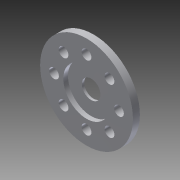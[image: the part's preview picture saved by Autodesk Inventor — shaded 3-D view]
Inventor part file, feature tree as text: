
AUTODESK INVENTOR PART (.ipt)
format: ipt  version: 2013 (Build 170138000, 138)  size: 110,592 bytes
history: native  units: mm
features: sketch x3, hole x2, extrude x1, pattern_circular x1
ambient origin geometry x8: Origin, YZ Plane, XZ Plane, XY Plane, X Axis, Y Axis, Z Axis, Center Point
feature tree (7):
  extrude  "押し出し2"  Depth=20.0mm
  hole  "穴2"  [1 undecoded]
  hole  "穴3"  [1 undecoded]
  pattern_circular  "円形状パターン2"  [2 undecoded]
  sketch  "スケッチ1"
  sketch  "スケッチ3"
  sketch  "スケッチ4"
note: 4 required parameter values undecoded (feature->parameter linkage not recoverable at this tier; creation-order binding heuristic only, values carry confidence <= 0.55)
